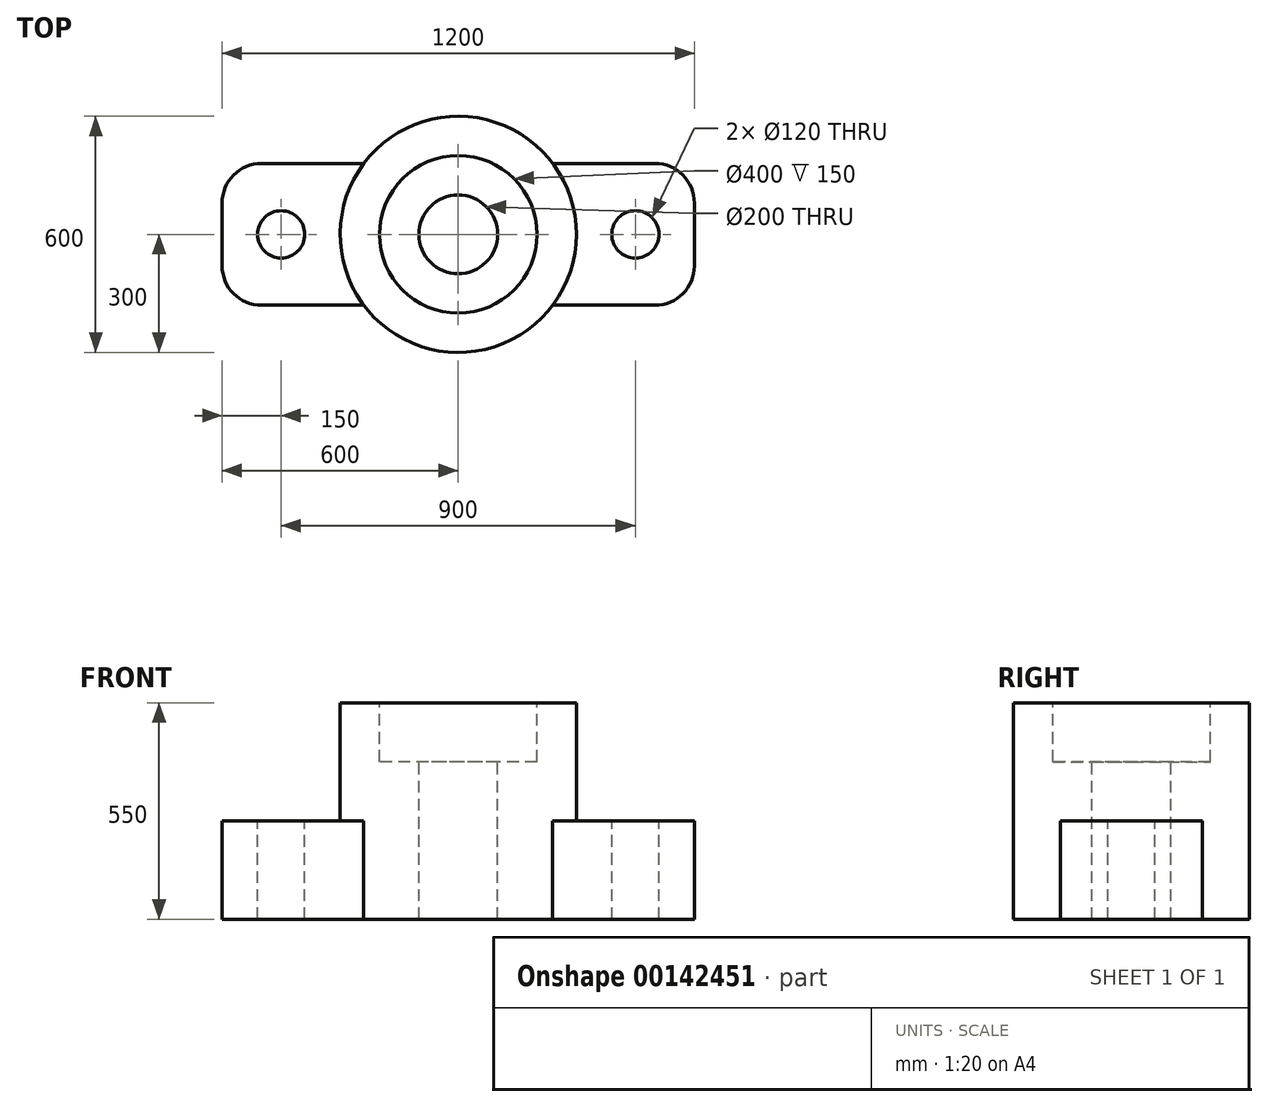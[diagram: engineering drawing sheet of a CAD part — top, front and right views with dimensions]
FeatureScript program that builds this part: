
annotation { "Feature Type Name" : "Feature", "Feature Type Description" : "" }
export const myFeature = defineFeature(function(context is Context, id is Id, definition is map)
    precondition{}
    {
        {
            var Q0;
            Q0=qCreatedBy(makeId("Top.planeOp"),FACE);
            var sketch = newSketch(context, id + "F0", { "sketchPlane" : qUnion([Q0])});
            skLineSegment(sketch, "E0.bottom", {"start": v(600, 180) * mm, "end": v(-600, 180) * mm});
            skLineSegment(sketch, "E0.top", {"start": v(600, -180) * mm, "end": v(-600, -180) * mm});
            skLineSegment(sketch, "E0.left", {"start": v(600, 180) * mm, "end": v(600, -180) * mm});
            skLineSegment(sketch, "E0.right", {"start": v(-600, 180) * mm, "end": v(-600, -180) * mm});
            skPoint(sketch, "E0.middle", {"position": v(0, 0) * mm});
            skSolve(sketch);
        }
        {
            var Q0;
            Q0 = qSketchRegion(id + "F0", true);
            extrude(context, id + "F1", {"entities" : qUnion([Q0]), "depth" : 250 * mm});
        }
        {
            var Q0;
            Q0=makeQuery(id+"F1.opExtrude","CAP_FACE",FACE,{"disambiguationData":[OSD([sQuery(id+"F0.wireOp",EDGE,"E0.bottom"),sQuery(id+"F0.wireOp",EDGE,"E0.top"),sQuery(id+"F0.wireOp",EDGE,"E0.left"),sQuery(id+"F0.wireOp",EDGE,"E0.right")])],"isStart":false});
            var sketch = newSketch(context, id + "F2", { "sketchPlane" : qUnion([Q0])});
            skCircle(sketch, "E1", {"center": v(-450, 0) * mm, "radius": 60 * mm});
            skCircle(sketch, "E2", {"center": v(450, 0) * mm, "radius": 60 * mm});
            skSolve(sketch);
        }
        {
            var Q0;
            Q0 = qSketchRegion(id + "F2", true);
            var Q1;
            Q1 = qSketchRegion(id + "F4", true);
            extrude(context, id + "F3", {"entities" : qUnion([Q0, Q1]), "operationType" : NewBodyOperationType.REMOVE, "endBound" : BoundingType.THROUGH_ALL, "oppositeDirection" : true, "depth" : 25 * mm});
        }
        {
            var Q0;
            Q0=makeQuery(id+"F1.opExtrude","CAP_FACE",FACE,{"disambiguationData":[OSD([sQuery(id+"F0.wireOp",EDGE,"E0.bottom"),sQuery(id+"F0.wireOp",EDGE,"E0.top"),sQuery(id+"F0.wireOp",EDGE,"E0.left"),sQuery(id+"F0.wireOp",EDGE,"E0.right")])],"isStart":false});
            var sketch = newSketch(context, id + "F4", { "sketchPlane" : qUnion([Q0])});
            skCircle(sketch, "E3", {"center": v(0, 0) * mm, "radius": 300 * mm});
            skSolve(sketch);
        }
        {
            var Q0;
            Q0 = qSketchRegion(id + "F4", true);
            extrude(context, id + "F5", {"entities" : qUnion([Q0]), "operationType" : NewBodyOperationType.REMOVE, "endBound" : BoundingType.THROUGH_ALL, "oppositeDirection" : true, "depth" : 25 * mm});
        }
        {
            var Q0;
            Q0=qCreatedBy(makeId("Top.planeOp"),FACE);
            var sketch = newSketch(context, id + "F6", { "sketchPlane" : qUnion([Q0])});
            skCircle(sketch, "E4", {"center": v(0, 0) * mm, "radius": 300 * mm});
            skSolve(sketch);
        }
        {
            var Q0;
            Q0 = qSketchRegion(id + "F6", true);
            extrude(context, id + "F7", {"entities" : qUnion([Q0]), "operationType" : NewBodyOperationType.ADD, "depth" : 550 * mm});
        }
        {
            var Q0;
            Q0=makeQuery(id+"F7.opExtrude","CAP_FACE",FACE,{"disambiguationData":[OSD([sQuery(id+"F6.wireOp",EDGE,"E4")])],"isStart":false});
            var sketch = newSketch(context, id + "F8", { "sketchPlane" : qUnion([Q0])});
            skCircle(sketch, "E5", {"center": v(0, 0) * mm, "radius": 200 * mm});
            skSolve(sketch);
        }
        {
            var Q0;
            Q0 = qSketchRegion(id + "F8", true);
            extrude(context, id + "F9", {"entities" : qUnion([Q0]), "operationType" : NewBodyOperationType.REMOVE, "oppositeDirection" : true, "depth" : 150 * mm});
        }
        {
            var Q0;
            Q0=makeQuery(id+"F9.boolean.opBoolean","COPY",FACE,{"derivedFrom":makeQuery(id+"F9.opExtrude","CAP_FACE",FACE,{"disambiguationData":[OSD([sQuery(id+"F8.wireOp",EDGE,"E5")])],"isStart":false})});
            var sketch = newSketch(context, id + "F10", { "sketchPlane" : qUnion([Q0])});
            skCircle(sketch, "E6", {"center": v(0, 0) * mm, "radius": 100 * mm});
            skSolve(sketch);
        }
        {
            var Q0;
            Q0 = qSketchRegion(id + "F10", true);
            extrude(context, id + "F11", {"entities" : qUnion([Q0]), "operationType" : NewBodyOperationType.REMOVE, "endBound" : BoundingType.THROUGH_ALL, "oppositeDirection" : true, "depth" : 25 * mm});
        }
        {
            var Q0;
            Q0=makeQuery(id+"F1.opExtrude","SWEPT_EDGE",EDGE,{"disambiguationData":[OSD([sQuery(id+"F0.wireOp",EDGE,"E0.top"),sQuery(id+"F0.wireOp",EDGE,"E0.right")])]});
            var Q1;
            Q1=makeQuery(id+"F1.opExtrude","SWEPT_EDGE",EDGE,{"disambiguationData":[OSD([sQuery(id+"F0.wireOp",EDGE,"E0.top"),sQuery(id+"F0.wireOp",EDGE,"E0.left")])]});
            var Q2;
            Q2=makeQuery(id+"F1.opExtrude","SWEPT_EDGE",EDGE,{"disambiguationData":[OSD([sQuery(id+"F0.wireOp",EDGE,"E0.bottom"),sQuery(id+"F0.wireOp",EDGE,"E0.left")])]});
            var Q3;
            Q3=makeQuery(id+"F1.opExtrude","SWEPT_EDGE",EDGE,{"disambiguationData":[OSD([sQuery(id+"F0.wireOp",EDGE,"E0.bottom"),sQuery(id+"F0.wireOp",EDGE,"E0.right")])]});
            fillet(context, id + "F12", {"entities" : qUnion([Q0, Q1, Q2, Q3]), "radius" : 100 * mm, "tangentPropagation" : true, "allowEdgeOverflow" : false});
        }
    });
